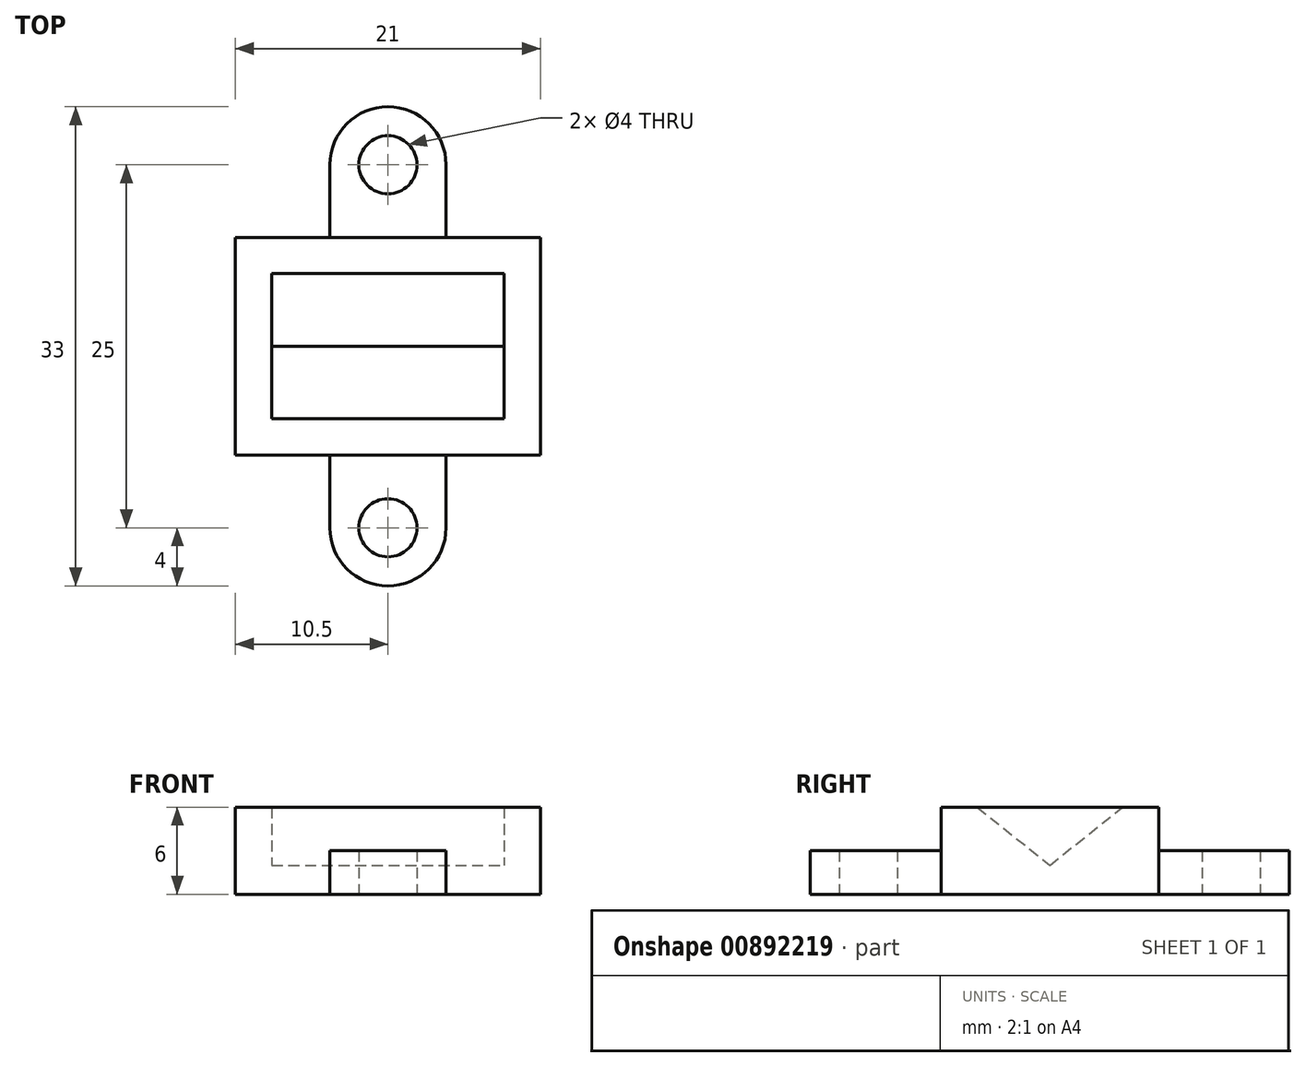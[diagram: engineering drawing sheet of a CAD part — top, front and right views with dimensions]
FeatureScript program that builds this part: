
annotation { "Feature Type Name" : "Feature", "Feature Type Description" : "" }
export const myFeature = defineFeature(function(context is Context, id is Id, definition is map)
    precondition{}
    {
        {
            var Q0;
            Q0=qCreatedBy(makeId("Top.planeOp"),FACE);
            var sketch = newSketch(context, id + "F0", { "sketchPlane" : qUnion([Q0])});
            skLineSegment(sketch, "E0.bottom", {"start": v(-10.5, 7.5) * mm, "end": v(10.5, 7.5) * mm});
            skLineSegment(sketch, "E0.top", {"start": v(-10.5, -7.5) * mm, "end": v(10.5, -7.5) * mm});
            skLineSegment(sketch, "E0.left", {"start": v(-10.5, 7.5) * mm, "end": v(-10.5, -7.5) * mm});
            skLineSegment(sketch, "E0.right", {"start": v(10.5, 7.5) * mm, "end": v(10.5, -7.5) * mm});
            skPoint(sketch, "E1", {"position": v(0, 7.5) * mm});
            skPoint(sketch, "E2", {"position": v(0, -7.5) * mm});
            skPoint(sketch, "E3", {"position": v(10.5, 0) * mm});
            skPoint(sketch, "E4", {"position": v(-10.5, 0) * mm});
            skSolve(sketch);
        }
        {
            var Q0;
            Q0 = qSketchRegion(id + "F0", true);
            extrude(context, id + "F1", {"entities" : qUnion([Q0]), "depth" : 6 * mm, "offsetDistance" : 25 * mm});
        }
        {
            var Q0;
            Q0=qCreatedBy(makeId("Right.planeOp"),FACE);
            var sketch = newSketch(context, id + "F2", { "sketchPlane" : qUnion([Q0])});
            skLineSegment(sketch, "E5", {"start": v(-5, 6) * mm, "end": v(0, 2) * mm});
            skLineSegment(sketch, "E6", {"start": v(0, 2) * mm, "end": v(5, 6) * mm});
            skLineSegment(sketch, "E7", {"start": v(5, 6) * mm, "end": v(-5, 6) * mm});
            skPoint(sketch, "E8", {"position": v(0, 6) * mm});
            skSolve(sketch);
        }
        {
            var Q0;
            Q0 = qSketchRegion(id + "F2", true);
            extrude(context, id + "F3", {"entities" : qUnion([Q0]), "operationType" : NewBodyOperationType.REMOVE, "endBound" : BoundingType.SYMMETRIC, "oppositeDirection" : true, "depth" : 16 * mm, "offsetDistance" : 25 * mm});
        }
        {
            var Q0;
            Q0=qCreatedBy(makeId("Top.planeOp"),FACE);
            var sketch = newSketch(context, id + "F4", { "sketchPlane" : qUnion([Q0])});
            skLineSegment(sketch, "E9.bottom", {"start": v(-4, 7.5) * mm, "end": v(4, 7.5) * mm});
            skLineSegment(sketch, "E9.left", {"start": v(-4, 7.5) * mm, "end": v(-4, 12.5) * mm});
            skLineSegment(sketch, "E9.right", {"start": v(4, 7.5) * mm, "end": v(4, 12.5) * mm});
            skPoint(sketch, "E10", {"position": v(0, 12.5) * mm});
            skArc(sketch, "E11", {"start": v(-4, 12.5) * mm, "mid": v(0, 16.5) * mm, "end": v(4, 12.5) * mm});
            skCircle(sketch, "E12", {"center": v(0, 12.5) * mm, "radius": 2 * mm});
            skPoint(sketch, "E13", {"position": v(0, 7.5) * mm});
            skLineSegment(sketch, "E14.MirrorCS", {"start": v(-4, -7.5) * mm, "end": v(-4, -12.5) * mm});
            skArc(sketch, "E15.MirrorCS", {"start": v(-4, -12.5) * mm, "mid": v(0, -16.5) * mm, "end": v(4, -12.5) * mm});
            skCircle(sketch, "E16.MirrorC", {"center": v(0, -12.5) * mm, "radius": 2 * mm});
            skLineSegment(sketch, "E17.MirrorCS", {"start": v(4, -7.5) * mm, "end": v(4, -12.5) * mm});
            skLineSegment(sketch, "E18.MirrorCS", {"start": v(-4, -7.5) * mm, "end": v(4, -7.5) * mm});
            skSolve(sketch);
        }
        {
            var Q0;
            Q0 = qSketchRegion(id + "F4", true);
            extrude(context, id + "F5", {"entities" : qUnion([Q0]), "operationType" : NewBodyOperationType.ADD, "depth" : 3 * mm, "offsetDistance" : 25 * mm});
        }
    });
